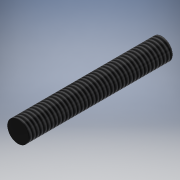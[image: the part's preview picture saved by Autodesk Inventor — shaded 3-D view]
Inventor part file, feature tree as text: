
AUTODESK INVENTOR PART (.ipt)
format: ipt  version: 2019 (Build 230136000, 136)  size: 100,864 bytes
history: native  units: mm
features: extrude x1, thread x1, sketch x1
ambient origin geometry x8: Origin, YZ Plane, XZ Plane, XY Plane, X Axis, Y Axis, Z Axis, Center Point
bodies: Solid1 (feature_tree)
feature tree (3):
  extrude  "Extrusion1"  Depth=27.0mm TaperAngle=0.0deg
  thread  "Thread1"  [1 undecoded]
  sketch  "Sketch1"  dims[d0=4.0mm d1=27.0mm d2=0.0mm d8=10.0mm d9=0.0mm]
note: 1 required parameter value undecoded (feature->parameter linkage not recoverable at this tier; creation-order binding heuristic only, values carry confidence <= 0.55)
